# Revit family: Видеосервер Синергет-L_RV17_LOD400
name_source: partatom
category: Электрооборудование
revit_build: Autodesk Revit 2017 (Build: 20170118_1100(x64)
units: mm (PartAtom-declared; Revit-internal decimal feet)

## family parameters
Всегда вертикально = Да
Конфигурация панели = Два столбца, слева направо
На основе рабочей плоскости = Нет
Общий = Нет
При загрузке вырезать с полостями = Нет
Размер круглого соединителя = Использовать диаметр
Тип детали = Щит
Точка расчета площади = Нет

## types (1)
- Сервер Синергет КСБО-L
    ADSK_URL страницы изделия = https://stilsoft.ru
    ADSK_Единица измерения = шт.
    ADSK_Завод-изготовитель = ООО «Основа Безопасности»
    ADSK_Количество = 0
    ADSK_Марка = СТВФ.426484.225
    ADSK_Масса = 14
    ADSK_Наименование = Видеосервер «Синергет-L»
    ADSK_Размер_Высота = 105 мм
    ADSK_Размер_Глубина = 573 мм
    ADSK_Размер_Ширина = 486 мм
    Время непрерывной работы = не ограничено
    Время приведения в рабочее состояние не более, мин. = 2
    Диапазон рабочих температур, С = от +5 до +50
5
0от +5 до +
5
от +5 до +50
    Количество входных аудиоканалов, шт. = 2
    Количество входных видеоканалов, шт. = 32
    Количество записываемых и передаваемых кадров/сек. = 25
    Мощность = 135
    Напряжение = 220
    Объем жесткого диска, ТБ = 30
    Оперативная память, ГБ = 8
    Поддерживаемые форматы сжатия = MPEG-4, H.264, H.265, VP-8, M-JPEG, THEORA, HEVC
    Ресурс до профилактического обслуживания не менее, ч = 4400
    Установленное программное обеспечение (1) = ОС «Astra Linux Common Edition»
    Установленное программное обеспечение (2) = Антивирус Касперского
    Установленное программное обеспечение (3) = СПО «Синергет КСБО»
